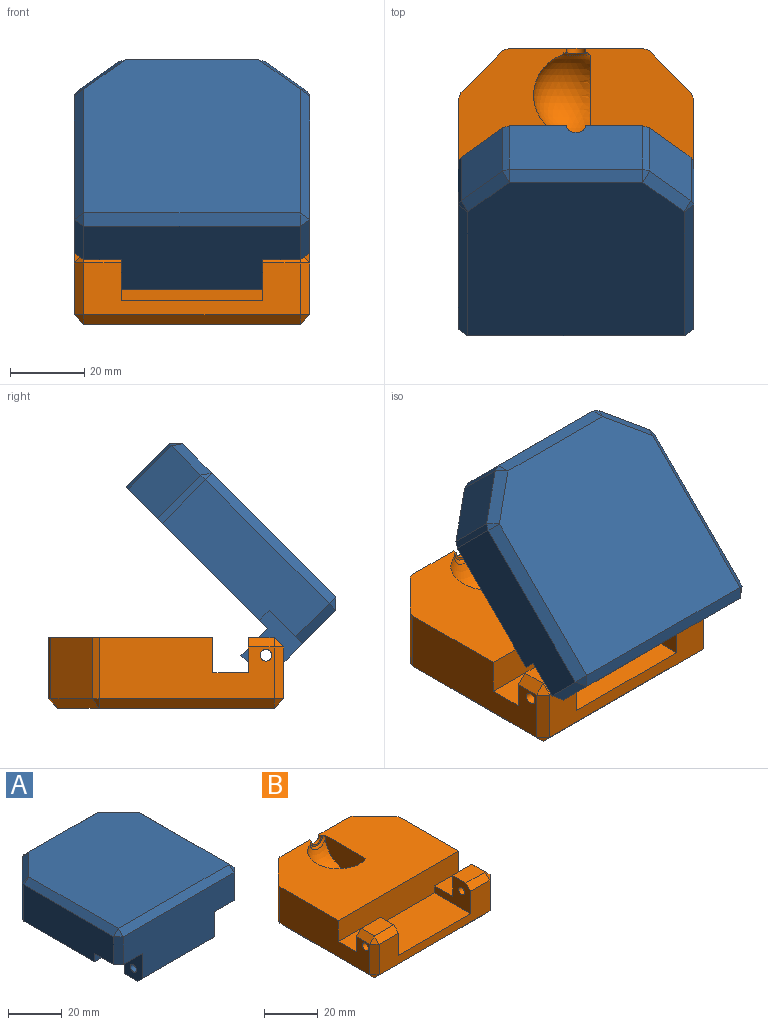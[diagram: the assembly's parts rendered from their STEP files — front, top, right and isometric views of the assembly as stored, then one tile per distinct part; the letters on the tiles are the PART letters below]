
ASSEMBLY  parts=2 mates=1
PART A: 41 faces, bbox 63.6x63.6x29.3 mm
  f0: plane 63.5x53.98mm, normal (0,0,-1), area 2885.7mm2, adj f2,f5,f7,f8,f10,f11,f20,f24
  f1: plane 38.1x6.99mm, normal (0,0,-1), area 266.1mm2, adj f4,f5,f31,f33
  f2: plane 47.21x16.51mm, normal (1,0,0), area 740.7mm2, adj f0,f3,f15,f20,f29,f30
  f3: plane 12.7x2.54mm, normal (0.71,-0.71,0), area 45.6mm2, adj f2,f6,f13,f30
  f4: plane 38.1x2.54mm, normal (0,-0.71,-0.71), area 136.9mm2, adj f1,f6,f31,f33
  f5: plane 38.1x10.16mm, normal (0,1,0), area 387.1mm2, adj f0,f1,f31,f33
  f6: plane 58.42x24.13mm, normal (0,-1,0), area 1177.4mm2, adj f3,f4,f12,f17,f30,f31,f33,f34
  f7: plane 36x16.51mm, normal (0,1,0), area 584.2mm2, adj f0,f22,f27,f28,f40
  f8: plane 47.21x16.51mm, normal (-1,0,0), area 740.7mm2, adj f0,f16,f17,f24,f32,f34
  f9: plane 58.42x58.42mm, normal (0,0,1), area 3287.2mm2, adj f12,f15,f16,f21,f22,f23
  f10: plane 16.51x11.21mm, normal (0.71,0.71,0), area 261.8mm2, adj f0,f20,f21,f27
  f11: plane 16.51x11.21mm, normal (-0.71,0.71,0), area 261.8mm2, adj f0,f23,f24,f28
  f12: plane 58.42x2.54mm, normal (0,-0.71,0.71), area 209.9mm2, adj f6,f9,f13,f14
  f13: plane 2.54x2.54mm, normal (0.58,-0.58,0.58), area 5.6mm2, adj f3,f12,f15
  f14: plane 2.54x2.54mm, normal (-0.58,-0.58,0.58), area 5.6mm2, adj f12,f16,f17
  f15: plane 47.21x2.54mm, normal (0.71,0,0.71), area 169.6mm2, adj f2,f9,f13,f18
  f16: plane 47.21x2.54mm, normal (-0.71,0,0.71), area 169.6mm2, adj f8,f9,f14,f19
  f17: plane 12.7x2.54mm, normal (-0.71,-0.71,0), area 45.6mm2, adj f6,f8,f14,f34
  f18: plane 2.54x2.54mm, normal (0.68,0.28,0.68), area 3.4mm2, adj f15,f20,f21
  f19: plane 2.54x2.54mm, normal (-0.68,0.28,0.68), area 3.4mm2, adj f16,f23,f24
  f20: plane 16.51x1.8mm, normal (0.92,0.38,0), area 32.1mm2, adj f0,f2,f10,f18
  f21: plane 13.01x13.01mm, normal (0.5,0.5,0.71), area 57mm2, adj f9,f10,f18,f25
  f22: plane 36x2.54mm, normal (0,0.71,0.71), area 129.3mm2, adj f7,f9,f25,f26
  f23: plane 13.01x13.01mm, normal (-0.5,0.5,0.71), area 57mm2, adj f9,f11,f19,f26
  f24: plane 16.51x1.8mm, normal (-0.92,0.38,0), area 32.1mm2, adj f0,f8,f11,f19
  f25: plane 2.54x2.54mm, normal (0.28,0.68,0.68), area 3.4mm2, adj f21,f22,f27
  f26: plane 2.54x2.54mm, normal (-0.28,0.68,0.68), area 3.4mm2, adj f22,f23,f28
  f27: plane 16.51x1.8mm, normal (0.38,0.92,0), area 32.1mm2, adj f0,f7,f10,f25
  f28: plane 16.51x1.8mm, normal (-0.38,0.92,0), area 32.1mm2, adj f0,f7,f11,f26
  f29: plane 12.7x3.81mm, normal (0,-1,0), area 48.4mm2, adj f0,f2,f30,f31
  f30: plane 12.7x12.7mm, normal (0,0,-1), area 158.1mm2, adj f2,f3,f6,f29,f31
  f31: plane 13.97x12.7mm, normal (1,0,0), area 134mm2, adj f0,f1,f4,f5,f6,f29,f30,f35
  f32: plane 12.7x3.81mm, normal (0,-1,0), area 48.4mm2, adj f0,f8,f33,f34
  f33: plane 13.97x12.7mm, normal (-1,0,0), area 134mm2, adj f0,f1,f4,f5,f6,f32,f34,f35
  f34: plane 12.7x12.7mm, normal (0,0,-1), area 158.1mm2, adj f6,f8,f17,f32,f33
  f35: cylinder r=1.59mm len=38.1mm, axis (1,0,0), area 380mm2, adj f31,f33
  f36: sphere r=11.43mm, area 521.8mm2, adj f0,f37,f38
  f37: torus R=4.98mm, axis (0,1,0), area 11mm2, adj f0,f36,f38,f39
  f38: plane 21.68x10.87mm, normal (-1,0,0), area 182.5mm2, adj f0,f36,f37
  f39: plane 6.48x3.24mm, normal (0,-1,0), area 6.3mm2, adj f0,f37,f40
  f40: cylinder r=2.54mm len=5.08mm, axis (0,1,0), area 10.5mm2, adj f0,f7,f39
PART B: 49 faces, bbox 63.7x63.7x19.3 mm
  f0: plane 63.5x44.45mm, normal (0,0,1), area 2361.4mm2, adj f1,f2,f6,f7,f12,f19,f20,f21
  f1: torus R=4.98mm, axis (0,-1,0), area 14mm2, adj f0,f45,f46,f47
  f2: plane 36x16.51mm, normal (0,1,0), area 584.2mm2, adj f0,f21,f23,f24,f48
  f3: plane 10.16x6.99mm, normal (0,0,1), area 71mm2, adj f9,f17,f27,f28
  f4: plane 58.42x13.97mm, normal (0,-1,0), area 429mm2, adj f9,f10,f11,f28,f35,f39,f40,f44
  f5: plane 10.16x6.99mm, normal (0,0,1), area 71mm2, adj f11,f15,f40,f41
  f6: plane 47.21x16.51mm, normal (1,0,0), area 663mm2, adj f0,f12,f13,f14,f15,f32,f38,f41
  f7: plane 47.21x16.51mm, normal (-1,0,0), area 663mm2, adj f0,f12,f16,f17,f18,f26,f27,f34
  f8: plane 58.42x58.42mm, normal (0,0,-1), area 3287.2mm2, adj f24,f25,f33,f34,f38,f39
  f9: plane 19.05x12.7mm, normal (1,0,0), area 140.1mm2, adj f3,f4,f10,f12,f16,f17,f18,f28
  f10: plane 38.1x19.05mm, normal (0,0,1), area 725.8mm2, adj f4,f9,f11,f12
  f11: plane 19.05x12.7mm, normal (-1,0,0), area 140.1mm2, adj f4,f5,f10,f12,f13,f14,f15,f40
  f12: plane 63.5x12.7mm, normal (0,-1,0), area 725.8mm2, adj f0,f6,f7,f9,f10,f11,f14,f18
  f13: cylinder r=1.59mm len=12.7mm, axis (1,0,0), area 126.7mm2, adj f6,f11
  f14: plane 12.7x9.53mm, normal (0,0,1), area 121mm2, adj f6,f11,f12,f15
  f15: plane 12.7x9.53mm, normal (0,1,0), area 117.7mm2, adj f5,f6,f11,f14,f41
  f16: cylinder r=1.59mm len=12.7mm, axis (1,0,0), area 126.7mm2, adj f7,f9
  f17: plane 12.7x9.53mm, normal (0,1,0), area 117.7mm2, adj f3,f7,f9,f18,f27
  f18: plane 12.7x9.53mm, normal (0,0,1), area 121mm2, adj f7,f9,f12,f17
  f19: plane 16.51x11.21mm, normal (0.71,0.71,0), area 261.8mm2, adj f0,f23,f32,f33
  f20: plane 16.51x11.21mm, normal (-0.71,0.71,0), area 261.8mm2, adj f0,f21,f25,f26
  f21: plane 16.51x1.8mm, normal (-0.38,0.92,0), area 32.1mm2, adj f0,f2,f20,f22
  f22: plane 2.54x2.54mm, normal (-0.28,0.68,-0.68), area 3.4mm2, adj f21,f24,f25
  f23: plane 16.51x1.8mm, normal (0.38,0.92,0), area 32.1mm2, adj f0,f2,f19,f29
  f24: plane 36x2.54mm, normal (0,0.71,-0.71), area 129.3mm2, adj f2,f8,f22,f29
  f25: plane 13.01x13.01mm, normal (-0.5,0.5,-0.71), area 57mm2, adj f8,f20,f22,f30
  f26: plane 16.51x1.8mm, normal (-0.92,0.38,0), area 32.1mm2, adj f0,f7,f20,f30
  f27: plane 6.99x2.54mm, normal (-0.71,0,0.71), area 25.1mm2, adj f3,f7,f17,f31
  f28: plane 10.16x2.54mm, normal (0,-0.71,0.71), area 36.5mm2, adj f3,f4,f9,f31
  f29: plane 2.54x2.54mm, normal (0.28,0.68,-0.68), area 3.4mm2, adj f23,f24,f33
  f30: plane 2.54x2.54mm, normal (-0.68,0.28,-0.68), area 3.4mm2, adj f25,f26,f34
  f31: plane 2.54x2.54mm, normal (-0.58,-0.58,0.58), area 5.6mm2, adj f27,f28,f35
  f32: plane 16.51x1.8mm, normal (0.92,0.38,0), area 32.1mm2, adj f0,f6,f19,f36
  f33: plane 13.01x13.01mm, normal (0.5,0.5,-0.71), area 57mm2, adj f8,f19,f29,f36
  f34: plane 47.21x2.54mm, normal (-0.71,0,-0.71), area 169.6mm2, adj f7,f8,f30,f37
  f35: plane 13.97x2.54mm, normal (-0.71,-0.71,0), area 50.2mm2, adj f4,f7,f31,f37
  f36: plane 2.54x2.54mm, normal (0.68,0.28,-0.68), area 3.4mm2, adj f32,f33,f38
  f37: plane 2.54x2.54mm, normal (-0.58,-0.58,-0.58), area 5.6mm2, adj f34,f35,f39
  f38: plane 47.21x2.54mm, normal (0.71,0,-0.71), area 169.6mm2, adj f6,f8,f36,f42
  f39: plane 58.42x2.54mm, normal (0,-0.71,-0.71), area 209.9mm2, adj f4,f8,f37,f42
  f40: plane 10.16x2.54mm, normal (0,-0.71,0.71), area 36.5mm2, adj f4,f5,f11,f43
  f41: plane 6.99x2.54mm, normal (0.71,0,0.71), area 25.1mm2, adj f5,f6,f15,f43
  f42: plane 2.54x2.54mm, normal (0.58,-0.58,-0.58), area 5.6mm2, adj f38,f39,f44
  f43: plane 2.54x2.54mm, normal (0.58,-0.58,0.58), area 5.6mm2, adj f40,f41,f44
  f44: plane 13.97x2.54mm, normal (0.71,-0.71,0), area 50.2mm2, adj f4,f6,f42,f43
  f45: sphere r=11.43mm, area 519mm2, adj f0,f1,f46
  f46: plane 21.83x11mm, normal (-1,0,0), area 182.5mm2, adj f0,f1,f45
  f47: plane 6.47x3.23mm, normal (0,-1,0), area 6.3mm2, adj f0,f1,f48
  f48: cylinder r=2.54mm len=5.08mm, axis (0,1,0), area 10.4mm2, adj f0,f2,f47
PLACE A rot(axis=(1,0,0),45deg) t=(0.02,8.74,-31.05)mm
PLACE B t=(0,24.63,-40.21)mm
MATE cylindrical A.f35 <-> B.f13  axis (1,0,0) through (-12.68,29.39,-44.97)mm
